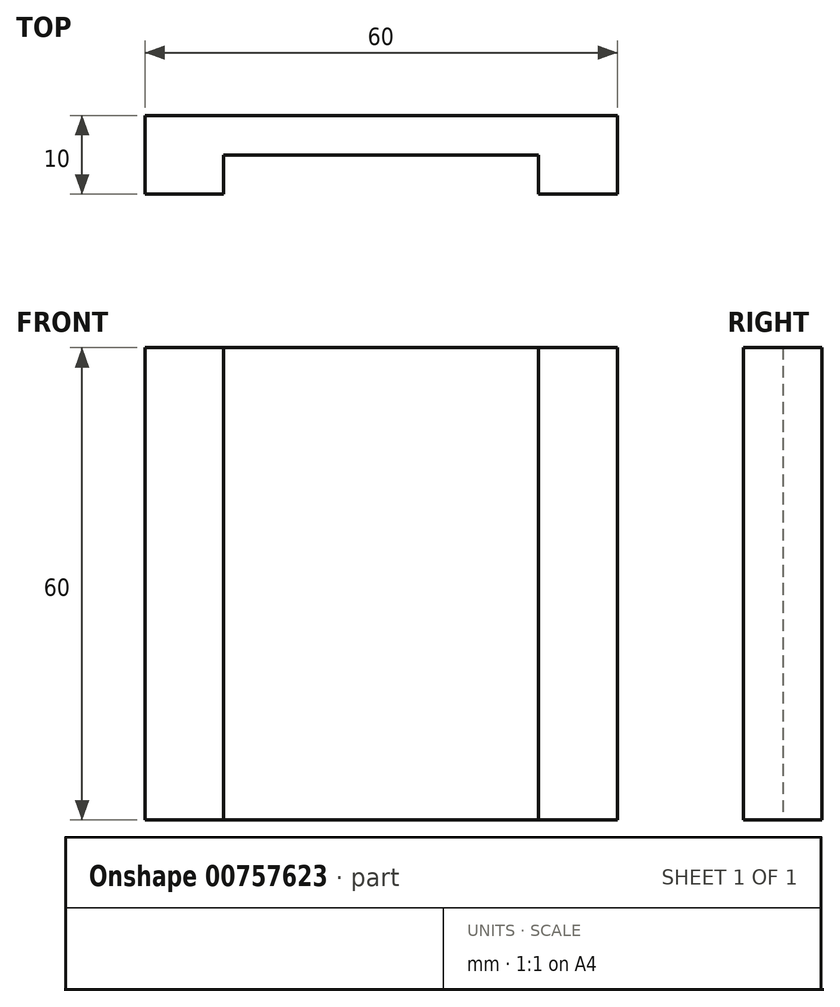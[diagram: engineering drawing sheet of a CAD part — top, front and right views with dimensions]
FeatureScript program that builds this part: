
annotation { "Feature Type Name" : "Feature", "Feature Type Description" : "" }
export const myFeature = defineFeature(function(context is Context, id is Id, definition is map)
    precondition{}
    {
        {
            var Q0;
            Q0=qCreatedBy(makeId("Top.planeOp"),FACE);
            var sketch = newSketch(context, id + "F0", { "sketchPlane" : qUnion([Q0])});
            skLineSegment(sketch, "E0.bottom", {"start": v(-30, -5) * mm, "end": v(-20, -5) * mm});
            skLineSegment(sketch, "E0.top", {"start": v(-30, 5) * mm, "end": v(30, 5) * mm});
            skLineSegment(sketch, "E0.left", {"start": v(-30, -5) * mm, "end": v(-30, 5) * mm});
            skLineSegment(sketch, "E0.right", {"start": v(30, -5) * mm, "end": v(30, 5) * mm});
            skLineSegment(sketch, "E1", {"start": v(-20, -5) * mm, "end": v(-20, 0) * mm});
            skLineSegment(sketch, "E2", {"start": v(-20, 0) * mm, "end": v(20, 0) * mm});
            skLineSegment(sketch, "E3", {"start": v(20, 0) * mm, "end": v(20, -5) * mm});
            skLineSegment(sketch, "E4.trimOffspring", {"start": v(20, -5) * mm, "end": v(30, -5) * mm});
            skSolve(sketch);
        }
        {
            var Q0;
            Q0=makeQuery(id+"F0.imprint","IMPRINT",FACE,{"disambiguationData":[TD([[makeQuery(id+"F0.imprint","IMPRINT",EDGE,{"derivedFrom":sQuery(id+"F0.wireOp",EDGE,"E0.bottom")}),1.0]])]});
            extrude(context, id + "F1", {"entities" : qUnion([Q0]), "depth" : 60 * mm, "offsetDistance" : 25 * mm});
        }
    });
